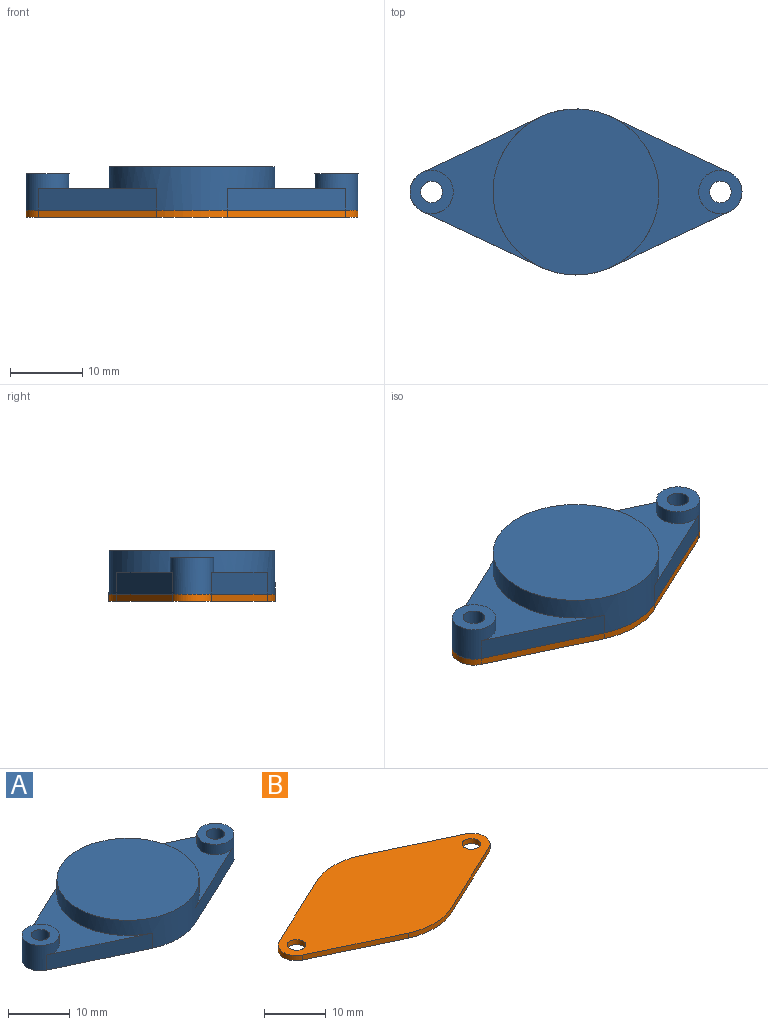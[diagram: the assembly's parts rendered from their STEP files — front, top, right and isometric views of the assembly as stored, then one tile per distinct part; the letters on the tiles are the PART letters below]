
ASSEMBLY  parts=2 mates=1
PART A: 17 faces, bbox 46x23x6 mm
  f0: plane 16.39x7.69mm, normal (0.42,0.91,0), area 54.3mm2, adj f2,f3,f4,f15
  f1: plane 16.39x7.69mm, normal (0.42,-0.91,0), area 54.3mm2, adj f2,f3,f4,f15
  f2: plane 20.82x16.39mm, normal (0,0,1), area 94.7mm2, adj f0,f1,f4,f15
  f3: plane 46x23mm, normal (0,0,-1), area 420.4mm2, adj f0,f1,f4,f6,f8,f9,f11,f12
  f4: cylinder r=11.5mm len=23mm, axis (0,0,-1), area 277.3mm2, adj f0,f1,f2,f3,f5,f11,f12,f13
  f5: plane 23x23mm, normal (0,0,1), area 415.5mm2, adj f4
  f6: cylinder r=8.5mm len=17mm, axis (0,0,-1), area 267mm2, adj f3,f7
  f7: plane 17x17mm, normal (0,0,-1), area 227mm2, adj f6
  f8: cylinder r=3mm len=6mm, axis (0,0,-1), area 58.1mm2, adj f3,f10,f11,f12,f13
  f9: cylinder r=1.5mm len=5mm, axis (0,0,-1), area 47.1mm2, adj f3,f10
  f10: plane 6x6mm, normal (0,0,1), area 21.2mm2, adj f8,f9
  f11: plane 16.39x7.69mm, normal (-0.42,0.91,0), area 54.3mm2, adj f3,f4,f8,f13
  f12: plane 16.39x7.69mm, normal (-0.42,-0.91,0), area 54.3mm2, adj f3,f4,f8,f13
  f13: plane 20.82x16.39mm, normal (0,0,1), area 94.7mm2, adj f4,f8,f11,f12
  f14: cylinder r=1.5mm len=5mm, axis (0,0,-1), area 47.1mm2, adj f3,f16
  f15: cylinder r=3mm len=6mm, axis (0,0,-1), area 58.1mm2, adj f0,f1,f2,f3,f16
  f16: plane 6x6mm, normal (0,0,1), area 21.2mm2, adj f14,f15
PART B: 12 faces, bbox 46x23x1 mm
  f0: cylinder r=3mm len=5.43mm, axis (0,0,-1), area 6.8mm2, adj f1,f7,f10,f11
  f1: plane 16.39x7.69mm, normal (-0.42,-0.91,0), area 18.1mm2, adj f0,f2,f10,f11
  f2: cylinder r=11.5mm len=9.78mm, axis (0,0,-1), area 10.1mm2, adj f1,f3,f10,f11
  f3: plane 16.39x7.69mm, normal (0.42,-0.91,0), area 18.1mm2, adj f2,f4,f10,f11
  f4: cylinder r=3mm len=5.43mm, axis (0,0,-1), area 6.8mm2, adj f3,f5,f10,f11
  f5: plane 16.39x7.69mm, normal (0.42,0.91,0), area 18.1mm2, adj f4,f6,f10,f11
  f6: cylinder r=11.5mm len=9.78mm, axis (0,0,-1), area 10.1mm2, adj f5,f7,f10,f11
  f7: plane 16.39x7.69mm, normal (-0.42,0.91,0), area 18.1mm2, adj f0,f6,f10,f11
  f8: cylinder r=1.5mm len=3mm, axis (0,0,-1), area 9.4mm2, adj f10,f11
  f9: cylinder r=1.5mm len=3mm, axis (0,0,-1), area 9.4mm2, adj f10,f11
  f10: plane 46x23mm, normal (0,0,1), area 647.4mm2, adj f0,f1,f2,f3,f4,f5,f6,f7
  f11: plane 46x23mm, normal (0,0,-1), area 647.4mm2, adj f0,f1,f2,f3,f4,f5,f6,f7
PLACE A at identity
PLACE B rot(axis=(1,0,0),180deg) t=(-0.06,0.01,0)mm
MATE fastened B.f2 <-> A.f4  axis (0,0,1) through (0,0,0)mm
